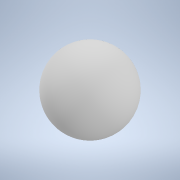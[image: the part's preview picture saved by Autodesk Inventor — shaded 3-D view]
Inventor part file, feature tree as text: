
AUTODESK INVENTOR PART (.ipt)
format: ipt  version: 2020 (Build 240168000, 168)  size: 116,224 bytes
history: native  units: in
note: dims shown in document units (in); Inventor stores cm internally (conversion verified against a paired STEP export)
features: revolve x1, sketch x1
ambient origin geometry x8: Origin, YZ Plane, XZ Plane, XY Plane, X Axis, Y Axis, Z Axis, Center Point
bodies: Solid1 (feature_tree)
feature tree (2):
  revolve  "Revolution1"  [1 undecoded]
  sketch  "Sketch1"  dims[d0=4.0in d1=2.0in d2=90.0deg]
note: 1 required parameter value undecoded (feature->parameter linkage not recoverable at this tier; creation-order binding heuristic only, values carry confidence <= 0.55)
